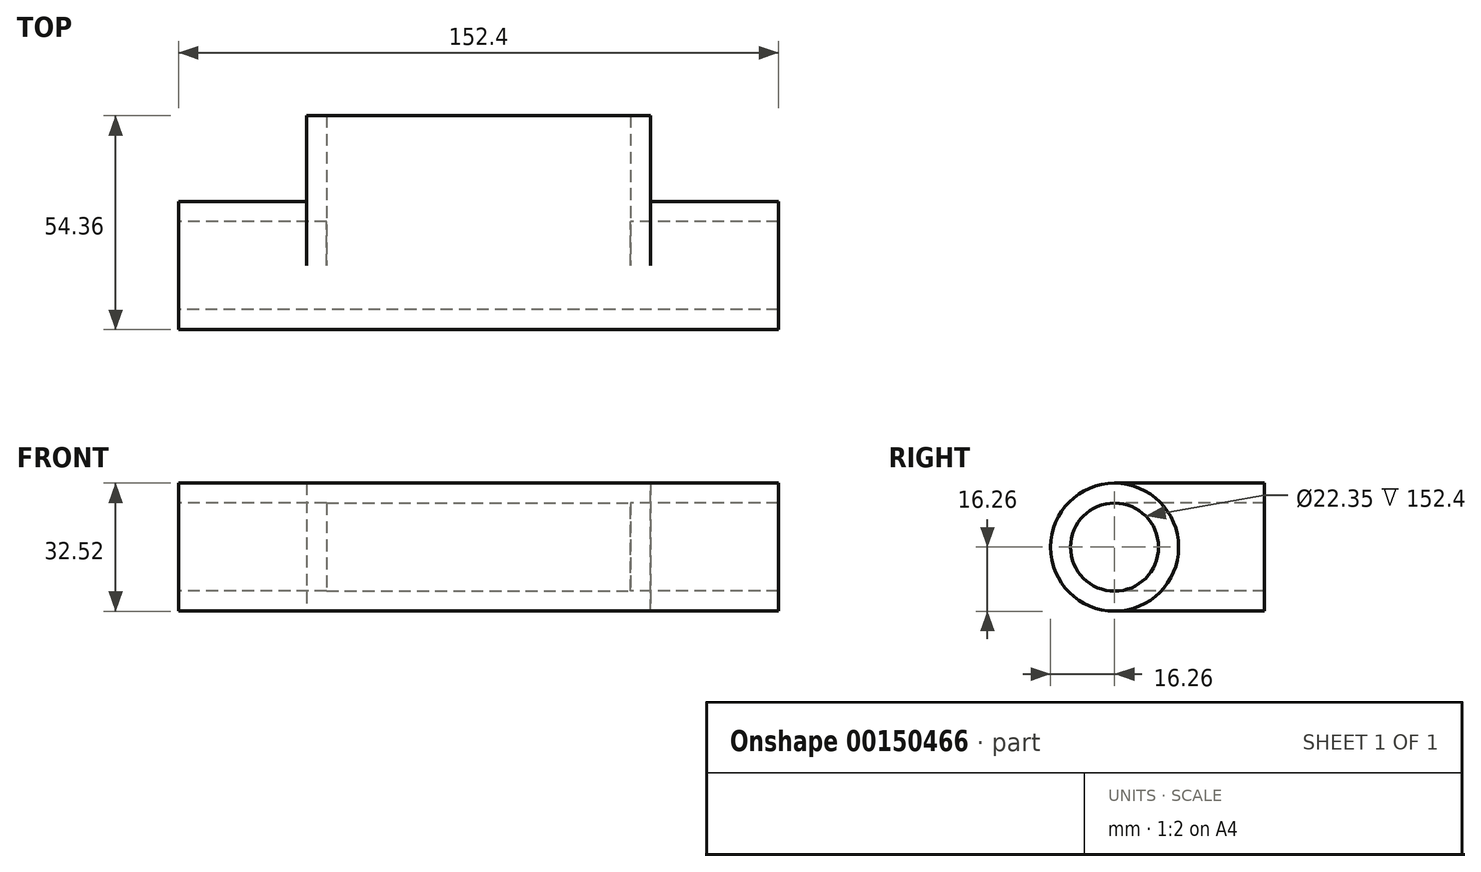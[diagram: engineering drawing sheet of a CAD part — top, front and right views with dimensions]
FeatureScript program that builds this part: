
annotation { "Feature Type Name" : "Feature", "Feature Type Description" : "" }
export const myFeature = defineFeature(function(context is Context, id is Id, definition is map)
    precondition{}
    {
        {
            var Q0;
            Q0=qCreatedBy(makeId("Top.planeOp"),FACE);
            var sketch = newSketch(context, id + "F0", { "sketchPlane" : qUnion([Q0])});
            skLineSegment(sketch, "E0.left", {"start": v(-76.2, 16.26) * mm, "end": v(-76.2, 11.18) * mm});
            skLineSegment(sketch, "E0.right", {"start": v(76.2, 16.26) * mm, "end": v(76.2, 11.18) * mm});
            skLineSegment(sketch, "E1", {"start": v(-34.44, 0) * mm, "end": v(24.74, 0) * mm});
            skLineSegment(sketch, "E2", {"start": v(-38.6, 16.26) * mm, "end": v(-38.6, 11.18) * mm});
            skLineSegment(sketch, "E3", {"start": v(38.6, 16.26) * mm, "end": v(38.6, 11.18) * mm});
            skLineSegment(sketch, "E4", {"start": v(-38.6, 16.26) * mm, "end": v(-76.2, 16.26) * mm});
            skLineSegment(sketch, "E5", {"start": v(38.6, 16.26) * mm, "end": v(76.2, 16.26) * mm});
            skLineSegment(sketch, "E6", {"start": v(-76.2, 11.18) * mm, "end": v(-38.6, 11.18) * mm});
            skLineSegment(sketch, "E7", {"start": v(38.6, 11.18) * mm, "end": v(76.2, 11.18) * mm});
            skSolve(sketch);
        }
        {
            var Q0;
            Q0=makeQuery(id+"F0.imprint","IMPRINT",FACE,{"disambiguationData":[TD([[makeQuery(id+"F0.imprint","IMPRINT",EDGE,{"derivedFrom":sQuery(id+"F0.wireOp",EDGE,"E0.left")}),1.0]])]});
            var Q1;
            Q1=makeQuery(id+"F0.imprint","IMPRINT",FACE,{"disambiguationData":[TD([[makeQuery(id+"F0.imprint","IMPRINT",EDGE,{"derivedFrom":sQuery(id+"F0.wireOp",EDGE,"E0.right")}),-1.0]])]});
            var Q2;
            Q2=sQuery(id+"F0.wireOp",EDGE,"E1");
            revolve(context, id + "F1", {"entities" : qUnion([Q0, Q1]), "axis" : qUnion([Q2]), "revolveType" : RevolveType.FULL});
        }
        {
            var Q0;
            Q0=qCreatedBy(makeId("Top.planeOp"),FACE);
            var sketch = newSketch(context, id + "F2", { "sketchPlane" : qUnion([Q0])});
            skLineSegment(sketch, "E8.MirrorCS", {"start": v(-38.6, -11.18) * mm, "end": v(38.6, -11.18) * mm});
            skLineSegment(sketch, "E9.MirrorCS", {"start": v(-38.6, -16.26) * mm, "end": v(38.6, -16.26) * mm});
            skLineSegment(sketch, "E10.MirrorCS", {"start": v(-38.6, -16.26) * mm, "end": v(-38.6, -11.18) * mm});
            skLineSegment(sketch, "E11.MirrorCS", {"start": v(38.6, -16.26) * mm, "end": v(38.6, -11.18) * mm});
            skLineSegment(sketch, "E12", {"start": v(-33, 0) * mm, "end": v(14.26, 0) * mm});
            skSolve(sketch);
        }
        {
            var Q0;
            Q0=makeQuery(id+"F2.imprint","IMPRINT",FACE,{"disambiguationData":[TD([[makeQuery(id+"F2.imprint","IMPRINT",EDGE,{"derivedFrom":sQuery(id+"F2.wireOp",EDGE,"E8.MirrorCS")}),-1.0]])]});
            var Q1;
            Q1=sQuery(id+"F2.wireOp",EDGE,"E12");
            revolve(context, id + "F3", {"entities" : qUnion([Q0]), "axis" : qUnion([Q1]), "revolveType" : RevolveType.SYMMETRIC, "angle" : 180 * degree});
        }
        {
            var Q0;
            Q0=qCreatedBy(makeId("Front.planeOp"),FACE);
            var sketch = newSketch(context, id + "F4", { "sketchPlane" : qUnion([Q0])});
            skLineSegment(sketch, "E13.bottom", {"start": v(38.6, 16.26) * mm, "end": v(-38.6, 16.26) * mm});
            skLineSegment(sketch, "E13.top", {"start": v(38.6, 11.18) * mm, "end": v(-38.6, 11.18) * mm});
            skLineSegment(sketch, "E13.left", {"start": v(38.6, 16.26) * mm, "end": v(38.6, 11.18) * mm});
            skLineSegment(sketch, "E13.right", {"start": v(-38.6, 16.26) * mm, "end": v(-38.6, 11.18) * mm});
            skLineSegment(sketch, "E14.MirrorCS", {"start": v(38.6, -11.18) * mm, "end": v(-38.6, -11.18) * mm});
            skLineSegment(sketch, "E15.MirrorCS", {"start": v(38.6, -16.26) * mm, "end": v(38.6, -11.18) * mm});
            skLineSegment(sketch, "E16.MirrorCS", {"start": v(-38.6, -16.26) * mm, "end": v(-38.6, -11.18) * mm});
            skLineSegment(sketch, "E17.MirrorCS", {"start": v(38.6, -16.26) * mm, "end": v(-38.6, -16.26) * mm});
            skSolve(sketch);
        }
        {
            var Q0;
            Q0=makeQuery(id+"F4.imprint","IMPRINT",FACE,{"disambiguationData":[TD([[makeQuery(id+"F4.imprint","IMPRINT",EDGE,{"derivedFrom":sQuery(id+"F4.wireOp",EDGE,"E13.bottom")}),1.0]])]});
            var Q1;
            Q1=makeQuery(id+"F4.imprint","IMPRINT",FACE,{"disambiguationData":[TD([[makeQuery(id+"F4.imprint","IMPRINT",EDGE,{"derivedFrom":sQuery(id+"F4.wireOp",EDGE,"E14.MirrorCS")}),1.0]])]});
            extrude(context, id + "F5", {"entities" : qUnion([Q0, Q1]), "oppositeDirection" : true, "depth" : 38.1 * mm});
        }
        {
            var Q0;
            Q0=makeQuery(id+"F1.opRevolve","SWEPT_FACE",FACE,{"disambiguationData":[OSD([sQuery(id+"F0.wireOp",EDGE,"E2")])]});
            var sketch = newSketch(context, id + "F6", { "sketchPlane" : qUnion([Q0])});
            skLineSegment(sketch, "E18.bottom", {"start": v(0, 16.26) * mm, "end": v(38.1, 16.26) * mm});
            skLineSegment(sketch, "E18.top", {"start": v(0, -16.26) * mm, "end": v(38.1, -16.26) * mm});
            skLineSegment(sketch, "E18.right", {"start": v(38.1, 16.26) * mm, "end": v(38.1, -16.26) * mm});
            skArc(sketch, "E19", {"start": v(0, -16.26) * mm, "mid": v(16.26, 0) * mm, "end": v(0, 16.26) * mm});
            skSolve(sketch);
        }
        {
            var Q0;
            Q0=makeQuery(id+"F6.imprint","IMPRINT",FACE,{"disambiguationData":[TD([[makeQuery(id+"F6.imprint","IMPRINT",EDGE,{"derivedFrom":sQuery(id+"F6.wireOp",EDGE,"E18.bottom")}),-1.0]])]});
            extrude(context, id + "F7", {"entities" : qUnion([Q0]), "operationType" : NewBodyOperationType.ADD, "oppositeDirection" : true, "depth" : 5.08 * mm});
        }
        {
            var Q0;
            Q0=makeQuery(id+"F1.opRevolve","SWEPT_FACE",FACE,{"disambiguationData":[OSD([sQuery(id+"F0.wireOp",EDGE,"E3")])]});
            var sketch = newSketch(context, id + "F8", { "sketchPlane" : qUnion([Q0])});
            skArc(sketch, "E20", {"start": v(0, 16.26) * mm, "mid": v(-16.26, 0) * mm, "end": v(0, -16.26) * mm});
            skLineSegment(sketch, "E21", {"start": v(0, -16.26) * mm, "end": v(-38.1, -16.26) * mm});
            skLineSegment(sketch, "E22", {"start": v(-38.1, -16.26) * mm, "end": v(-38.1, 16.26) * mm});
            skLineSegment(sketch, "E23", {"start": v(-38.1, 16.26) * mm, "end": v(0, 16.26) * mm});
            skSolve(sketch);
        }
        {
            var Q0;
            Q0=makeQuery(id+"F8.imprint","IMPRINT",FACE,{"disambiguationData":[TD([[makeQuery(id+"F8.imprint","IMPRINT",EDGE,{"derivedFrom":sQuery(id+"F8.wireOp",EDGE,"E20")}),-1.0]])]});
            extrude(context, id + "F9", {"entities" : qUnion([Q0]), "operationType" : NewBodyOperationType.ADD, "oppositeDirection" : true, "depth" : 5.08 * mm});
        }
    });
